# Revit family: НЕВАТОМ_Диффузор КВ_20220407
name_source: partatom
category: Воздухораспределители
revit_build: Autodesk Revit 2017 (Build: 20170118_1100(x64)
units: mm (PartAtom-declared; Revit-internal decimal feet)

## family parameters
Всегда вертикально = Да
На основе рабочей плоскости = Нет
Общий = Нет
При загрузке вырезать с полостями = Нет
Размер круглого соединителя = Использовать диаметр
Тип детали = Нормальный
Точка расчета площади = Нет

## types (4) — shared parameters
ADSK_Единица измерения = шт.
ADSK_Завод-изготовитель = NEVATOM
ADSK_Материал наименование = Алюминий
ADSK_Наименование = КЛАПАН ВЫТЯЖНОЙ
Nevatom_URL = https://t.me
p = 15 мм
Ключевая пометка = Вентиляция
Корпус = Пластмасса, непрозрачная, белая
Материал = Сталь серая

## per-type parameters (varying)
| type | 0.25*A | A | ADSK_Масса | ADSK_Масса_Текст | ADSK_Размер_Высота | ADSK_Размер_Длина | ADSK_Размер_Ширина | D | D-6 | d | d/2 | d1 | ΔPmax | ΔPmin | Макс. расход | Макс. расход воздуха | Мин. расход | Минимальный расход воздуха |
| КВ 100 | 12 мм | 47 мм | 0.29 | 0,29 | 77 мм | 137 мм | 137 мм | 100 мм | 94 мм | 140 мм | 70 мм | 137 мм | 230.0 Па | 35.0 Па | 100.0 м³/ч | 100.0 м³/ч | 18.0 м³/ч | 18.0 м³/ч |
| КВ 125 | 12 мм | 49 мм | 0.35 | 0,35 | 79 мм | 164 мм | 164 мм | 125 мм | 119 мм | 165 мм | 83 мм | 164 мм | 140.0 Па | 50.0 Па | 170.0 м³/ч | 170.0 м³/ч | 60.0 м³/ч | 60.0 м³/ч |
| КВ 160 | 15 мм | 60 мм | 0.65 | 0,65 | 90 мм | 212 мм | 212 мм | 160 мм | 154 мм | 200 мм | 100 мм | 212 мм | 140.0 Па | 40.0 Па | 190.0 м³/ч | 190.0 м³/ч | 65.0 м³/ч | 65.0 м³/ч |
| КВ 200 | 19 мм | 75 мм | 0.85 | 0,85 | 105 мм | 248 мм | 248 мм | 200 мм | 194 мм | 240 мм | 120 мм | 248 мм | 140.0 Па | 30.0 Па | 330.0 м³/ч | 330.0 м³/ч | 65.0 м³/ч | 65.0 м³/ч |

note: column(s) folded — value = type name in every type: ADSK_Марка
